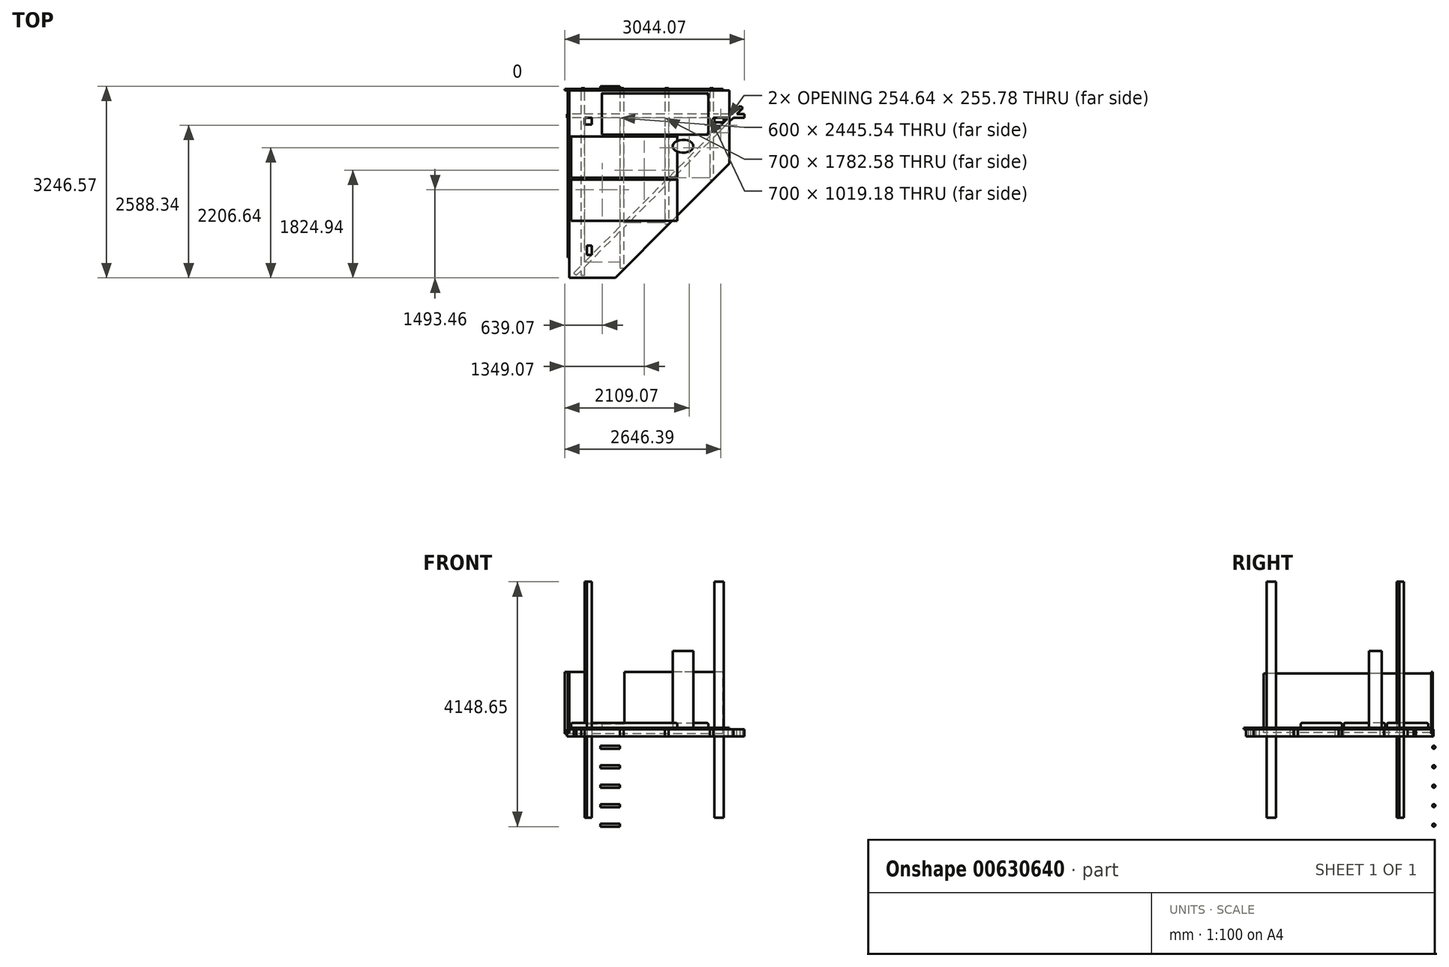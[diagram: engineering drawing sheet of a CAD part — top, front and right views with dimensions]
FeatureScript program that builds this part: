
annotation { "Feature Type Name" : "Feature", "Feature Type Description" : "" }
export const myFeature = defineFeature(function(context is Context, id is Id, definition is map)
    precondition{}
    {
        {
            var Q0;
            Q0=qCreatedBy(makeId("Top.planeOp"),FACE);
            var sketch = newSketch(context, id + "F0", { "sketchPlane" : qUnion([Q0])});
            skLineSegment(sketch, "E0.bottom", {"start": v(0, 0) * mm, "end": v(120, 0) * mm});
            skLineSegment(sketch, "E0.top", {"start": v(0, -120) * mm, "end": v(120, -120) * mm});
            skLineSegment(sketch, "E0.left", {"start": v(0, 0) * mm, "end": v(0, -120) * mm});
            skLineSegment(sketch, "E0.right", {"start": v(120, 0) * mm, "end": v(120, -120) * mm});
            skLineSegment(sketch, "E1.bottom", {"start": v(2200, 0) * mm, "end": v(2355, 0) * mm});
            skLineSegment(sketch, "E1.top", {"start": v(2200, -80) * mm, "end": v(2355, -80) * mm});
            skLineSegment(sketch, "E1.left", {"start": v(2200, 0) * mm, "end": v(2200, -80) * mm});
            skLineSegment(sketch, "E1.right", {"start": v(2355, 0) * mm, "end": v(2355, -80) * mm});
            skLineSegment(sketch, "E2.bottom", {"start": v(40, -2170) * mm, "end": v(120, -2170) * mm});
            skLineSegment(sketch, "E2.top", {"start": v(40, -2325) * mm, "end": v(120, -2325) * mm});
            skLineSegment(sketch, "E2.left", {"start": v(40, -2170) * mm, "end": v(40, -2325) * mm});
            skLineSegment(sketch, "E2.right", {"start": v(120, -2170) * mm, "end": v(120, -2325) * mm});
            skSolve(sketch);
        }
        {
            var Q0;
            Q0=makeQuery(id+"F0.imprint","IMPRINT",FACE,{"disambiguationData":[TD([[makeQuery(id+"F0.imprint","IMPRINT",EDGE,{"derivedFrom":sQuery(id+"F0.wireOp",EDGE,"E2.bottom")}),-1.0]])]});
            var Q1;
            Q1=makeQuery(id+"F0.imprint","IMPRINT",FACE,{"disambiguationData":[TD([[makeQuery(id+"F0.imprint","IMPRINT",EDGE,{"derivedFrom":sQuery(id+"F0.wireOp",EDGE,"E0.bottom")}),-1.0]])]});
            var Q2;
            Q2=makeQuery(id+"F0.imprint","IMPRINT",FACE,{"disambiguationData":[TD([[makeQuery(id+"F0.imprint","IMPRINT",EDGE,{"derivedFrom":sQuery(id+"F0.wireOp",EDGE,"E1.bottom")}),-1.0]])]});
            extrude(context, id + "F1", {"entities" : qUnion([Q0, Q1, Q2]), "depth" : 4000 * mm, "offsetDistance" : 25 * mm});
        }
        {
            var Q0;
            Q0=qCreatedBy(makeId("Top.planeOp"),FACE);
            cPlane(context, id + "F2", {"entities" : qUnion([Q0]), "cplaneType" : CPlaneType.OFFSET, "offset" : 1500 * mm, "width" : 150 * mm, "height" : 150 * mm});
        }
        {
            var Q0;
            Q0=qCreatedBy(id+"F2.planeOp",FACE);
            var sketch = newSketch(context, id + "F3", { "sketchPlane" : qUnion([Q0])});
            skLineSegment(sketch, "E3.bottom", {"start": v(0, -2675) * mm, "end": v(-60, -2675) * mm});
            skLineSegment(sketch, "E3.top", {"start": v(0, 500) * mm, "end": v(-60, 500) * mm});
            skLineSegment(sketch, "E3.left", {"start": v(0, -2675) * mm, "end": v(0, 500) * mm});
            skLineSegment(sketch, "E3.right", {"start": v(-60, -2675) * mm, "end": v(-60, 500) * mm});
            skLineSegment(sketch, "E4.bottom", {"start": v(2705, 0) * mm, "end": v(-300, 0) * mm});
            skLineSegment(sketch, "E4.top", {"start": v(2705, 60) * mm, "end": v(-300, 60) * mm});
            skLineSegment(sketch, "E4.left", {"start": v(2705, 0) * mm, "end": v(2705, 60) * mm});
            skLineSegment(sketch, "E4.right", {"start": v(-300, 0) * mm, "end": v(-300, 60) * mm});
            skLineSegment(sketch, "E5", {"start": v(-182.52, -2628.87) * mm, "end": v(2636.07, 202.33) * mm});
            skLineSegment(sketch, "E6", {"start": v(2636.07, 202.33) * mm, "end": v(2678.6, 160) * mm});
            skLineSegment(sketch, "E7", {"start": v(2678.6, 160) * mm, "end": v(-140, -2671.2) * mm});
            skLineSegment(sketch, "E8", {"start": v(-182.52, -2628.87) * mm, "end": v(-140, -2671.2) * mm});
            skLineSegment(sketch, "E9.bottom", {"start": v(600, 500) * mm, "end": v(660, 500) * mm});
            skLineSegment(sketch, "E9.top", {"start": v(600, -2550) * mm, "end": v(660, -2550) * mm});
            skLineSegment(sketch, "E9.left", {"start": v(600, 500) * mm, "end": v(600, -2550) * mm});
            skLineSegment(sketch, "E9.right", {"start": v(660, 500) * mm, "end": v(660, -2550) * mm});
            skLineSegment(sketch, "E10.bottom", {"start": v(1360, 500) * mm, "end": v(1420, 500) * mm});
            skLineSegment(sketch, "E10.top", {"start": v(1360, -1800) * mm, "end": v(1420, -1800) * mm});
            skLineSegment(sketch, "E10.left", {"start": v(1360, 500) * mm, "end": v(1360, -1800) * mm});
            skLineSegment(sketch, "E10.right", {"start": v(1420, 500) * mm, "end": v(1420, -1800) * mm});
            skLineSegment(sketch, "E11.bottom", {"start": v(2120, 500) * mm, "end": v(2180, 500) * mm});
            skLineSegment(sketch, "E11.top", {"start": v(2120, -1050) * mm, "end": v(2180, -1050) * mm});
            skLineSegment(sketch, "E11.left", {"start": v(2120, 500) * mm, "end": v(2120, -1050) * mm});
            skLineSegment(sketch, "E11.right", {"start": v(2180, 500) * mm, "end": v(2180, -1050) * mm});
            skLineSegment(sketch, "E12", {"start": v(487.83, -2749.25) * mm, "end": v(2859.35, -367.12) * mm, "construction": true});
            skSolve(sketch);
        }
        {
            var Q0;
            {var subQ0=sQuery(id+"F3.wireOp",EDGE,"E7");var subQ1=sQuery(id+"F3.wireOp",EDGE,"E3.left");var subQ2=makeQuery(id+"F3.imprint","INTERSECT",VERTEX,{"derivedFrom":[subQ1,subQ0]});Q0=makeQuery(id+"F3.imprint","IMPRINT",FACE,{"disambiguationData":[TD([[makeQuery(id+"F3.imprint","IMPRINT",EDGE,{"disambiguationData":[TD([[subQ2,-1.0]])],"derivedFrom":subQ1}),1.0]])]});}
            var Q1;
            {var subQ0=sQuery(id+"F3.wireOp",EDGE,"E3.bottom");Q1=makeQuery(id+"F3.imprint","IMPRINT",FACE,{"disambiguationData":[TD([[makeQuery(id+"F3.imprint","IMPRINT",EDGE,{"derivedFrom":subQ0}),-1.0]])]});}
            var Q2;
            {var subQ5=sQuery(id+"F3.wireOp",EDGE,"E8");Q2=makeQuery(id+"F3.imprint","IMPRINT",FACE,{"disambiguationData":[TD([[makeQuery(id+"F3.imprint","IMPRINT",EDGE,{"derivedFrom":subQ5}),1.0]])]});}
            var Q3;
            {var subQ0=sQuery(id+"F3.wireOp",EDGE,"E7");var subQ1=sQuery(id+"F3.wireOp",EDGE,"E3.left");var subQ2=makeQuery(id+"F3.imprint","INTERSECT",VERTEX,{"derivedFrom":[subQ1,subQ0]});Q3=makeQuery(id+"F3.imprint","IMPRINT",FACE,{"disambiguationData":[TD([[makeQuery(id+"F3.imprint","IMPRINT",EDGE,{"disambiguationData":[TD([[subQ2,-1.0]])],"derivedFrom":subQ1}),-1.0]])]});}
            var Q4;
            {var subQ0=sQuery(id+"F3.wireOp",EDGE,"E5");var subQ1=sQuery(id+"F3.wireOp",EDGE,"E3.left");var subQ2=makeQuery(id+"F3.imprint","INTERSECT",VERTEX,{"derivedFrom":[subQ1,subQ0]});Q4=makeQuery(id+"F3.imprint","IMPRINT",FACE,{"disambiguationData":[TD([[makeQuery(id+"F3.imprint","IMPRINT",EDGE,{"disambiguationData":[TD([[subQ2,-1.0]])],"derivedFrom":subQ1}),1.0]])]});}
            var Q5;
            {var subQ0=sQuery(id+"F3.wireOp",EDGE,"E4.top");var subQ1=sQuery(id+"F3.wireOp",EDGE,"E3.left");var subQ2=makeQuery(id+"F3.imprint","INTERSECT",VERTEX,{"derivedFrom":[subQ1,subQ0]});Q5=makeQuery(id+"F3.imprint","IMPRINT",FACE,{"disambiguationData":[TD([[makeQuery(id+"F3.imprint","IMPRINT",EDGE,{"disambiguationData":[TD([[subQ2,1.0]])],"derivedFrom":subQ1}),-1.0]])]});}
            var Q6;
            {var subQ0=sQuery(id+"F3.wireOp",EDGE,"E4.left");Q6=makeQuery(id+"F3.imprint","IMPRINT",FACE,{"disambiguationData":[TD([[makeQuery(id+"F3.imprint","IMPRINT",EDGE,{"derivedFrom":subQ0}),1.0]])]});}
            var Q7;
            {var subQ5=sQuery(id+"F3.wireOp",EDGE,"E6");Q7=makeQuery(id+"F3.imprint","IMPRINT",FACE,{"disambiguationData":[TD([[makeQuery(id+"F3.imprint","IMPRINT",EDGE,{"derivedFrom":subQ5}),-1.0]])]});}
            var Q8;
            {var subQ0=sQuery(id+"F3.wireOp",EDGE,"E7");var subQ1=sQuery(id+"F3.wireOp",EDGE,"E4.bottom");var subQ2=makeQuery(id+"F3.imprint","INTERSECT",VERTEX,{"derivedFrom":[subQ1,subQ0]});Q8=makeQuery(id+"F3.imprint","IMPRINT",FACE,{"disambiguationData":[TD([[makeQuery(id+"F3.imprint","IMPRINT",EDGE,{"disambiguationData":[TD([[subQ2,-1.0]])],"derivedFrom":subQ1}),-1.0]])]});}
            var Q9;
            {var subQ0=sQuery(id+"F3.wireOp",EDGE,"E3.top");Q9=makeQuery(id+"F3.imprint","IMPRINT",FACE,{"disambiguationData":[TD([[makeQuery(id+"F3.imprint","IMPRINT",EDGE,{"derivedFrom":subQ0}),1.0]])]});}
            var Q10;
            {var subQ5=sQuery(id+"F3.wireOp",EDGE,"E4.right");Q10=makeQuery(id+"F3.imprint","IMPRINT",FACE,{"disambiguationData":[TD([[makeQuery(id+"F3.imprint","IMPRINT",EDGE,{"derivedFrom":subQ5}),-1.0]])]});}
            var Q11;
            {var subQ0=sQuery(id+"F3.wireOp",EDGE,"E4.top");var subQ1=sQuery(id+"F3.wireOp",EDGE,"E3.left");var subQ2=makeQuery(id+"F3.imprint","INTERSECT",VERTEX,{"derivedFrom":[subQ1,subQ0]});Q11=makeQuery(id+"F3.imprint","IMPRINT",FACE,{"disambiguationData":[TD([[makeQuery(id+"F3.imprint","IMPRINT",EDGE,{"disambiguationData":[TD([[subQ2,1.0]])],"derivedFrom":subQ1}),1.0]])]});}
            var Q12;
            {var subQ0=sQuery(id+"F3.wireOp",EDGE,"E9.right");var subQ1=sQuery(id+"F3.wireOp",EDGE,"E4.bottom");var subQ2=makeQuery(id+"F3.imprint","INTERSECT",VERTEX,{"derivedFrom":[subQ1,subQ0]});Q12=makeQuery(id+"F3.imprint","IMPRINT",FACE,{"disambiguationData":[TD([[makeQuery(id+"F3.imprint","IMPRINT",EDGE,{"disambiguationData":[TD([[subQ2,-1.0]])],"derivedFrom":subQ1}),1.0]])]});}
            var Q13;
            {var subQ5=sQuery(id+"F3.wireOp",EDGE,"E9.top");Q13=makeQuery(id+"F3.imprint","IMPRINT",FACE,{"disambiguationData":[TD([[makeQuery(id+"F3.imprint","IMPRINT",EDGE,{"derivedFrom":subQ5}),1.0]])]});}
            var Q14;
            {var subQ5=sQuery(id+"F3.wireOp",EDGE,"E10.top");Q14=makeQuery(id+"F3.imprint","IMPRINT",FACE,{"disambiguationData":[TD([[makeQuery(id+"F3.imprint","IMPRINT",EDGE,{"derivedFrom":subQ5}),1.0]])]});}
            var Q15;
            {var subQ0=sQuery(id+"F3.wireOp",EDGE,"E10.right");var subQ1=sQuery(id+"F3.wireOp",EDGE,"E4.bottom");var subQ2=makeQuery(id+"F3.imprint","INTERSECT",VERTEX,{"derivedFrom":[subQ1,subQ0]});Q15=makeQuery(id+"F3.imprint","IMPRINT",FACE,{"disambiguationData":[TD([[makeQuery(id+"F3.imprint","IMPRINT",EDGE,{"disambiguationData":[TD([[subQ2,-1.0]])],"derivedFrom":subQ1}),1.0]])]});}
            var Q16;
            {var subQ0=sQuery(id+"F3.wireOp",EDGE,"E9.right");var subQ1=sQuery(id+"F3.wireOp",EDGE,"E5");var subQ2=makeQuery(id+"F3.imprint","INTERSECT",VERTEX,{"derivedFrom":[subQ1,subQ0]});Q16=makeQuery(id+"F3.imprint","IMPRINT",FACE,{"disambiguationData":[TD([[makeQuery(id+"F3.imprint","IMPRINT",EDGE,{"disambiguationData":[TD([[subQ2,-1.0]])],"derivedFrom":subQ1}),-1.0]])]});}
            var Q17;
            {var subQ0=sQuery(id+"F3.wireOp",EDGE,"E10.right");var subQ1=sQuery(id+"F3.wireOp",EDGE,"E5");var subQ2=makeQuery(id+"F3.imprint","INTERSECT",VERTEX,{"derivedFrom":[subQ1,subQ0]});Q17=makeQuery(id+"F3.imprint","IMPRINT",FACE,{"disambiguationData":[TD([[makeQuery(id+"F3.imprint","IMPRINT",EDGE,{"disambiguationData":[TD([[subQ2,-1.0]])],"derivedFrom":subQ1}),-1.0]])]});}
            var Q18;
            {var subQ5=sQuery(id+"F3.wireOp",EDGE,"E11.top");Q18=makeQuery(id+"F3.imprint","IMPRINT",FACE,{"disambiguationData":[TD([[makeQuery(id+"F3.imprint","IMPRINT",EDGE,{"derivedFrom":subQ5}),1.0]])]});}
            var Q19;
            {var subQ0=sQuery(id+"F3.wireOp",EDGE,"E9.left");var subQ1=sQuery(id+"F3.wireOp",EDGE,"E5");var subQ2=makeQuery(id+"F3.imprint","INTERSECT",VERTEX,{"derivedFrom":[subQ1,subQ0]});Q19=makeQuery(id+"F3.imprint","IMPRINT",FACE,{"disambiguationData":[TD([[makeQuery(id+"F3.imprint","IMPRINT",EDGE,{"disambiguationData":[TD([[subQ2,-1.0]])],"derivedFrom":subQ1}),-1.0]])]});}
            var Q20;
            {var subQ0=sQuery(id+"F3.wireOp",EDGE,"E10.left");var subQ1=sQuery(id+"F3.wireOp",EDGE,"E5");var subQ2=makeQuery(id+"F3.imprint","INTERSECT",VERTEX,{"derivedFrom":[subQ1,subQ0]});Q20=makeQuery(id+"F3.imprint","IMPRINT",FACE,{"disambiguationData":[TD([[makeQuery(id+"F3.imprint","IMPRINT",EDGE,{"disambiguationData":[TD([[subQ2,-1.0]])],"derivedFrom":subQ1}),-1.0]])]});}
            var Q21;
            {var subQ0=sQuery(id+"F3.wireOp",EDGE,"E11.left");var subQ1=sQuery(id+"F3.wireOp",EDGE,"E5");var subQ2=makeQuery(id+"F3.imprint","INTERSECT",VERTEX,{"derivedFrom":[subQ1,subQ0]});Q21=makeQuery(id+"F3.imprint","IMPRINT",FACE,{"disambiguationData":[TD([[makeQuery(id+"F3.imprint","IMPRINT",EDGE,{"disambiguationData":[TD([[subQ2,-1.0]])],"derivedFrom":subQ1}),-1.0]])]});}
            var Q22;
            {var subQ0=sQuery(id+"F3.wireOp",EDGE,"E7");var subQ1=sQuery(id+"F3.wireOp",EDGE,"E4.bottom");var subQ2=makeQuery(id+"F3.imprint","INTERSECT",VERTEX,{"derivedFrom":[subQ1,subQ0]});Q22=makeQuery(id+"F3.imprint","IMPRINT",FACE,{"disambiguationData":[TD([[makeQuery(id+"F3.imprint","IMPRINT",EDGE,{"disambiguationData":[TD([[subQ2,-1.0]])],"derivedFrom":subQ1}),1.0]])]});}
            var Q23;
            {var subQ0=sQuery(id+"F3.wireOp",EDGE,"E5");var subQ1=sQuery(id+"F3.wireOp",EDGE,"E4.bottom");var subQ2=makeQuery(id+"F3.imprint","INTERSECT",VERTEX,{"derivedFrom":[subQ1,subQ0]});Q23=makeQuery(id+"F3.imprint","IMPRINT",FACE,{"disambiguationData":[TD([[makeQuery(id+"F3.imprint","IMPRINT",EDGE,{"disambiguationData":[TD([[subQ2,-1.0]])],"derivedFrom":subQ1}),-1.0]])]});}
            var Q24;
            {var subQ0=sQuery(id+"F3.wireOp",EDGE,"E11.right");var subQ1=sQuery(id+"F3.wireOp",EDGE,"E4.bottom");var subQ2=makeQuery(id+"F3.imprint","INTERSECT",VERTEX,{"derivedFrom":[subQ1,subQ0]});Q24=makeQuery(id+"F3.imprint","IMPRINT",FACE,{"disambiguationData":[TD([[makeQuery(id+"F3.imprint","IMPRINT",EDGE,{"disambiguationData":[TD([[subQ2,-1.0]])],"derivedFrom":subQ1}),-1.0]])]});}
            var Q25;
            {var subQ0=sQuery(id+"F3.wireOp",EDGE,"E11.right");var subQ1=sQuery(id+"F3.wireOp",EDGE,"E4.bottom");var subQ2=makeQuery(id+"F3.imprint","INTERSECT",VERTEX,{"derivedFrom":[subQ1,subQ0]});Q25=makeQuery(id+"F3.imprint","IMPRINT",FACE,{"disambiguationData":[TD([[makeQuery(id+"F3.imprint","IMPRINT",EDGE,{"disambiguationData":[TD([[subQ2,-1.0]])],"derivedFrom":subQ1}),1.0]])]});}
            var Q26;
            {var subQ5=sQuery(id+"F3.wireOp",EDGE,"E11.bottom");Q26=makeQuery(id+"F3.imprint","IMPRINT",FACE,{"disambiguationData":[TD([[makeQuery(id+"F3.imprint","IMPRINT",EDGE,{"derivedFrom":subQ5}),-1.0]])]});}
            var Q27;
            {var subQ5=sQuery(id+"F3.wireOp",EDGE,"E10.bottom");Q27=makeQuery(id+"F3.imprint","IMPRINT",FACE,{"disambiguationData":[TD([[makeQuery(id+"F3.imprint","IMPRINT",EDGE,{"derivedFrom":subQ5}),-1.0]])]});}
            var Q28;
            {var subQ0=sQuery(id+"F3.wireOp",EDGE,"E10.right");var subQ1=sQuery(id+"F3.wireOp",EDGE,"E4.bottom");var subQ2=makeQuery(id+"F3.imprint","INTERSECT",VERTEX,{"derivedFrom":[subQ1,subQ0]});Q28=makeQuery(id+"F3.imprint","IMPRINT",FACE,{"disambiguationData":[TD([[makeQuery(id+"F3.imprint","IMPRINT",EDGE,{"disambiguationData":[TD([[subQ2,-1.0]])],"derivedFrom":subQ1}),-1.0]])]});}
            var Q29;
            {var subQ0=sQuery(id+"F3.wireOp",EDGE,"E10.left");var subQ1=sQuery(id+"F3.wireOp",EDGE,"E4.bottom");var subQ2=makeQuery(id+"F3.imprint","INTERSECT",VERTEX,{"derivedFrom":[subQ1,subQ0]});Q29=makeQuery(id+"F3.imprint","IMPRINT",FACE,{"disambiguationData":[TD([[makeQuery(id+"F3.imprint","IMPRINT",EDGE,{"disambiguationData":[TD([[subQ2,-1.0]])],"derivedFrom":subQ1}),-1.0]])]});}
            var Q30;
            {var subQ0=sQuery(id+"F3.wireOp",EDGE,"E9.right");var subQ1=sQuery(id+"F3.wireOp",EDGE,"E4.bottom");var subQ2=makeQuery(id+"F3.imprint","INTERSECT",VERTEX,{"derivedFrom":[subQ1,subQ0]});Q30=makeQuery(id+"F3.imprint","IMPRINT",FACE,{"disambiguationData":[TD([[makeQuery(id+"F3.imprint","IMPRINT",EDGE,{"disambiguationData":[TD([[subQ2,-1.0]])],"derivedFrom":subQ1}),-1.0]])]});}
            var Q31;
            {var subQ5=sQuery(id+"F3.wireOp",EDGE,"E9.bottom");Q31=makeQuery(id+"F3.imprint","IMPRINT",FACE,{"disambiguationData":[TD([[makeQuery(id+"F3.imprint","IMPRINT",EDGE,{"derivedFrom":subQ5}),-1.0]])]});}
            var Q32;
            {var subQ0=sQuery(id+"F3.wireOp",EDGE,"E11.left");var subQ1=sQuery(id+"F3.wireOp",EDGE,"E4.bottom");var subQ2=makeQuery(id+"F3.imprint","INTERSECT",VERTEX,{"derivedFrom":[subQ1,subQ0]});Q32=makeQuery(id+"F3.imprint","IMPRINT",FACE,{"disambiguationData":[TD([[makeQuery(id+"F3.imprint","IMPRINT",EDGE,{"disambiguationData":[TD([[subQ2,-1.0]])],"derivedFrom":subQ1}),-1.0]])]});}
            extrude(context, id + "F4", {"entities" : qUnion([Q0, Q1, Q2, Q3, Q4, Q5, Q6, Q7, Q8, Q9, Q10, Q11, Q12, Q13, Q14, Q15, Q16, Q17, Q18, Q19, Q20, Q21, Q22, Q23, Q24, Q25, Q26, Q27, Q28, Q29, Q30, Q31, Q32]), "oppositeDirection" : true, "depth" : 120 * mm, "offsetDistance" : 25 * mm});
        }
        {
            var Q0;
            Q0=makeQuery(id+"F4.opExtrude","CAP_FACE",FACE,{"disambiguationData":[OSD([sQuery(id+"F3.wireOp",EDGE,"E3.bottom"),sQuery(id+"F3.wireOp",EDGE,"E3.top"),sQuery(id+"F3.wireOp",EDGE,"E3.left"),sQuery(id+"F3.wireOp",EDGE,"E3.right"),sQuery(id+"F3.wireOp",EDGE,"E4.bottom"),sQuery(id+"F3.wireOp",EDGE,"E4.top"),sQuery(id+"F3.wireOp",EDGE,"E4.left"),sQuery(id+"F3.wireOp",EDGE,"E4.right"),sQuery(id+"F3.wireOp",EDGE,"E5"),sQuery(id+"F3.wireOp",EDGE,"E6"),sQuery(id+"F3.wireOp",EDGE,"E7"),sQuery(id+"F3.wireOp",EDGE,"E8")])],"isStart":true});
            var sketch = newSketch(context, id + "F5", { "sketchPlane" : qUnion([Q0])});
            skLineSegment(sketch, "E13", {"start": v(-260, 460) * mm, "end": v(-260, -2716.23) * mm});
            skLineSegment(sketch, "E14", {"start": v(-260, -2716.23) * mm, "end": v(520.71, -2716.23) * mm});
            skLineSegment(sketch, "E15", {"start": v(520.71, -2716.23) * mm, "end": v(2450.2, -778.11) * mm});
            skLineSegment(sketch, "E16", {"start": v(-260, 460) * mm, "end": v(2450.2, 460) * mm});
            skLineSegment(sketch, "E17", {"start": v(2450.2, 460) * mm, "end": v(2450.2, -778.11) * mm});
            skSolve(sketch);
        }
        {
            var Q0;
            {var subQ0=sQuery(id+"F5.wireOp",EDGE,"E16");var subQ1=sQuery(id+"F5.wireOp",EDGE,"E13");var subQ2=makeQuery(id+"F5.imprint","INTERSECT",VERTEX,{"derivedFrom":[subQ1,subQ0]});Q0=makeQuery(id+"F5.imprint","IMPRINT",FACE,{"disambiguationData":[TD([[makeQuery(id+"F5.imprint","IMPRINT",EDGE,{"disambiguationData":[TD([[subQ2,-1.0]])],"derivedFrom":subQ1}),1.0]])]});}
            var Q1;
            {var subQ0=sQuery(id+"F3.wireOp",EDGE,"E4.right");var subQ8=sQuery(id+"F5.wireOp",EDGE,"E13");var subQ17=sQuery(id+"F3.wireOp",EDGE,"E4.top");var subQ19=makeQuery(id+"F4.opExtrude","CAP_EDGE",EDGE,{"disambiguationData":[OSD([subQ17]),TDD([makeQuery(id+"F3.imprint","IMPRINT",EDGE,{"disambiguationData":[TD([[makeQuery(id+"F3.imprint","INTERSECT",VERTEX,{"derivedFrom":[subQ17,subQ0]}),1.0]])],"derivedFrom":subQ17})])],"isStart":true});var subQ33=makeQuery(id+"F5.imprint","INTERSECT",VERTEX,{"derivedFrom":[subQ19,subQ8]});Q1=makeQuery(id+"F5.imprint","IMPRINT",FACE,{"disambiguationData":[TD([[makeQuery(id+"F5.imprint","IMPRINT",EDGE,{"disambiguationData":[TD([[subQ33,-1.0]])],"derivedFrom":subQ8}),1.0]])]});}
            var Q2;
            {var subQ0=sQuery(id+"F5.wireOp",EDGE,"E17");var subQ1=sQuery(id+"F5.wireOp",EDGE,"E16");var subQ2=makeQuery(id+"F5.imprint","INTERSECT",VERTEX,{"derivedFrom":[subQ1,subQ0]});Q2=makeQuery(id+"F5.imprint","IMPRINT",FACE,{"disambiguationData":[TD([[makeQuery(id+"F5.imprint","IMPRINT",EDGE,{"disambiguationData":[TD([[subQ2,1.0]])],"derivedFrom":subQ1}),-1.0]])]});}
            var Q3;
            {var subQ0=sQuery(id+"F5.wireOp",EDGE,"E14");var subQ1=sQuery(id+"F5.wireOp",EDGE,"E13");var subQ2=makeQuery(id+"F5.imprint","INTERSECT",VERTEX,{"derivedFrom":[subQ1,subQ0]});Q3=makeQuery(id+"F5.imprint","IMPRINT",FACE,{"disambiguationData":[TD([[makeQuery(id+"F5.imprint","IMPRINT",EDGE,{"disambiguationData":[TD([[subQ2,1.0]])],"derivedFrom":subQ1}),1.0]])]});}
            var Q4;
            {var subQ0=sQuery(id+"F5.wireOp",EDGE,"E15");Q4=makeQuery(id+"F5.imprint","IMPRINT",FACE,{"disambiguationData":[TD([[makeQuery(id+"F5.imprint","IMPRINT",EDGE,{"derivedFrom":subQ0}),1.0]])]});}
            var Q5;
            {var subQ1=sQuery(id+"F3.wireOp",EDGE,"E3.left");var subQ3=sQuery(id+"F3.wireOp",EDGE,"E5");var subQ6=makeQuery(id+"F3.imprint","INTERSECT",VERTEX,{"derivedFrom":[subQ1,subQ3]});var subQ7=makeQuery(id+"F4.opExtrude","CAP_EDGE",EDGE,{"disambiguationData":[OSD([subQ1]),TDD([makeQuery(id+"F3.imprint","IMPRINT",EDGE,{"disambiguationData":[TD([[subQ6,-1.0]])],"derivedFrom":subQ1})])],"isStart":true});var subQ9=sQuery(id+"F5.wireOp",EDGE,"E14");var subQ10=makeQuery(id+"F5.imprint","INTERSECT",VERTEX,{"derivedFrom":[subQ7,subQ9]});Q5=makeQuery(id+"F5.imprint","IMPRINT",FACE,{"disambiguationData":[TD([[makeQuery(id+"F5.imprint","IMPRINT",EDGE,{"disambiguationData":[TD([[subQ10,-1.0]])],"derivedFrom":subQ9}),1.0]])]});}
            var Q6;
            {var subQ0=sQuery(id+"F5.wireOp",EDGE,"E14");var subQ1=sQuery(id+"F3.wireOp",EDGE,"E7");var subQ2=sQuery(id+"F3.wireOp",EDGE,"E3.left");var subQ4=makeQuery(id+"F4.opExtrude","CAP_EDGE",EDGE,{"disambiguationData":[OSD([subQ1]),TDD([makeQuery(id+"F3.imprint","IMPRINT",EDGE,{"disambiguationData":[TD([[makeQuery(id+"F3.imprint","INTERSECT",VERTEX,{"derivedFrom":[subQ2,subQ1]}),1.0]])],"derivedFrom":subQ1})])],"isStart":true});var subQ5=makeQuery(id+"F5.imprint","INTERSECT",VERTEX,{"derivedFrom":[subQ4,subQ0]});Q6=makeQuery(id+"F5.imprint","IMPRINT",FACE,{"disambiguationData":[TD([[makeQuery(id+"F5.imprint","IMPRINT",EDGE,{"disambiguationData":[TD([[subQ5,1.0]])],"derivedFrom":subQ0}),1.0]])]});}
            var Q7;
            {var subQ1=sQuery(id+"F3.wireOp",EDGE,"E7");var subQ4=sQuery(id+"F3.wireOp",EDGE,"E10.left");var subQ5=makeQuery(id+"F3.imprint","INTERSECT",VERTEX,{"derivedFrom":[subQ1,subQ4]});var subQ6=makeQuery(id+"F4.opExtrude","CAP_EDGE",EDGE,{"disambiguationData":[OSD([subQ1]),TDD([makeQuery(id+"F3.imprint","IMPRINT",EDGE,{"disambiguationData":[TD([[subQ5,-1.0]])],"derivedFrom":subQ1})])],"isStart":true});Q7=makeQuery(id+"F5.imprint","IMPRINT",FACE,{"disambiguationData":[TD([[makeQuery(id+"F5.imprint","IMPRINT",EDGE,{"derivedFrom":subQ6}),1.0]])]});}
            var Q8;
            {var subQ0=sQuery(id+"F5.wireOp",EDGE,"E14");var subQ1=sQuery(id+"F3.wireOp",EDGE,"E7");var subQ4=makeQuery(id+"F4.opExtrude","CAP_EDGE",EDGE,{"disambiguationData":[OSD([subQ1]),TDD([makeQuery(id+"F3.imprint","IMPRINT",EDGE,{"disambiguationData":[TD([[makeQuery(id+"F3.imprint","INTERSECT",VERTEX,{"derivedFrom":[sQuery(id+"F3.wireOp",EDGE,"E3.left"),subQ1]}),1.0]])],"derivedFrom":subQ1})])],"isStart":true});var subQ5=makeQuery(id+"F5.imprint","INTERSECT",VERTEX,{"derivedFrom":[subQ4,subQ0]});Q8=makeQuery(id+"F5.imprint","IMPRINT",FACE,{"disambiguationData":[TD([[makeQuery(id+"F5.imprint","IMPRINT",EDGE,{"disambiguationData":[TD([[subQ5,-1.0]])],"derivedFrom":subQ0}),1.0]])]});}
            var Q9;
            {var subQ0=sQuery(id+"F3.wireOp",EDGE,"E10.left");var subQ1=sQuery(id+"F3.wireOp",EDGE,"E4.bottom");var subQ2=makeQuery(id+"F3.imprint","INTERSECT",VERTEX,{"derivedFrom":[subQ1,subQ0]});Q9=makeQuery(id+"F5.imprint","IMPRINT",FACE,{"disambiguationData":[TD([[makeQuery(id+"F5.imprint","IMPRINT",EDGE,{"derivedFrom":makeQuery(id+"F4.opExtrude","CAP_EDGE",EDGE,{"disambiguationData":[OSD([subQ1]),TDD([makeQuery(id+"F3.imprint","IMPRINT",EDGE,{"disambiguationData":[TD([[subQ2,-1.0]])],"derivedFrom":subQ1})])],"isStart":true})}),1.0]])]});}
            var Q10;
            {var subQ0=sQuery(id+"F3.wireOp",EDGE,"E11.left");var subQ1=sQuery(id+"F3.wireOp",EDGE,"E4.bottom");var subQ2=makeQuery(id+"F3.imprint","INTERSECT",VERTEX,{"derivedFrom":[subQ1,subQ0]});Q10=makeQuery(id+"F5.imprint","IMPRINT",FACE,{"disambiguationData":[TD([[makeQuery(id+"F5.imprint","IMPRINT",EDGE,{"derivedFrom":makeQuery(id+"F4.opExtrude","CAP_EDGE",EDGE,{"disambiguationData":[OSD([subQ1]),TDD([makeQuery(id+"F3.imprint","IMPRINT",EDGE,{"disambiguationData":[TD([[subQ2,-1.0]])],"derivedFrom":subQ1})])],"isStart":true})}),1.0]])]});}
            var Q11;
            {var subQ2=sQuery(id+"F3.wireOp",EDGE,"E4.top");var subQ6=sQuery(id+"F3.wireOp",EDGE,"E11.left");var subQ7=makeQuery(id+"F3.imprint","INTERSECT",VERTEX,{"derivedFrom":[subQ2,subQ6]});var subQ10=makeQuery(id+"F4.opExtrude","CAP_EDGE",EDGE,{"disambiguationData":[OSD([subQ2]),TDD([makeQuery(id+"F3.imprint","IMPRINT",EDGE,{"disambiguationData":[TD([[subQ7,-1.0]])],"derivedFrom":subQ2})])],"isStart":true});Q11=makeQuery(id+"F5.imprint","IMPRINT",FACE,{"disambiguationData":[TD([[makeQuery(id+"F5.imprint","IMPRINT",EDGE,{"derivedFrom":subQ10}),-1.0]])]});}
            var Q12;
            {var subQ2=sQuery(id+"F3.wireOp",EDGE,"E4.top");var subQ6=sQuery(id+"F3.wireOp",EDGE,"E10.left");var subQ7=makeQuery(id+"F3.imprint","INTERSECT",VERTEX,{"derivedFrom":[subQ2,subQ6]});var subQ10=makeQuery(id+"F4.opExtrude","CAP_EDGE",EDGE,{"disambiguationData":[OSD([subQ2]),TDD([makeQuery(id+"F3.imprint","IMPRINT",EDGE,{"disambiguationData":[TD([[subQ7,-1.0]])],"derivedFrom":subQ2})])],"isStart":true});Q12=makeQuery(id+"F5.imprint","IMPRINT",FACE,{"disambiguationData":[TD([[makeQuery(id+"F5.imprint","IMPRINT",EDGE,{"derivedFrom":subQ10}),-1.0]])]});}
            var Q13;
            {var subQ1=sQuery(id+"F3.wireOp",EDGE,"E3.left");var subQ2=sQuery(id+"F3.wireOp",EDGE,"E4.top");var subQ3=makeQuery(id+"F3.imprint","INTERSECT",VERTEX,{"derivedFrom":[subQ1,subQ2]});var subQ10=makeQuery(id+"F4.opExtrude","CAP_EDGE",EDGE,{"disambiguationData":[OSD([subQ2]),TDD([makeQuery(id+"F3.imprint","IMPRINT",EDGE,{"disambiguationData":[TD([[subQ3,1.0]])],"derivedFrom":subQ2})])],"isStart":true});Q13=makeQuery(id+"F5.imprint","IMPRINT",FACE,{"disambiguationData":[TD([[makeQuery(id+"F5.imprint","IMPRINT",EDGE,{"derivedFrom":subQ10}),-1.0]])]});}
            var Q14;
            {var subQ0=sQuery(id+"F3.wireOp",EDGE,"E5");var subQ1=sQuery(id+"F3.wireOp",EDGE,"E3.left");var subQ2=makeQuery(id+"F3.imprint","INTERSECT",VERTEX,{"derivedFrom":[subQ1,subQ0]});Q14=makeQuery(id+"F5.imprint","IMPRINT",FACE,{"disambiguationData":[TD([[makeQuery(id+"F5.imprint","IMPRINT",EDGE,{"derivedFrom":makeQuery(id+"F4.opExtrude","CAP_EDGE",EDGE,{"disambiguationData":[OSD([subQ1]),TDD([makeQuery(id+"F3.imprint","IMPRINT",EDGE,{"disambiguationData":[TD([[subQ2,-1.0]])],"derivedFrom":subQ1})])],"isStart":true})}),-1.0]])]});}
            extrude(context, id + "F6", {"entities" : qUnion([Q0, Q1, Q2, Q3, Q4, Q5, Q6, Q7, Q8, Q9, Q10, Q11, Q12, Q13, Q14]), "depth" : 25 * mm, "offsetDistance" : 25 * mm});
        }
        {
            var Q0;
            Q0=makeQuery(id+"F6.opExtrude","CAP_FACE",FACE,{"disambiguationData":[OSD([sQuery(id+"F5.wireOp",EDGE,"E13"),sQuery(id+"F5.wireOp",EDGE,"E14"),sQuery(id+"F5.wireOp",EDGE,"E15"),sQuery(id+"F5.wireOp",EDGE,"E16"),sQuery(id+"F5.wireOp",EDGE,"E17")])],"isStart":false});
            var sketch = newSketch(context, id + "F7", { "sketchPlane" : qUnion([Q0])});
            skLineSegment(sketch, "E18.bottom", {"start": v(292.62, 410) * mm, "end": v(2092.62, 410) * mm});
            skLineSegment(sketch, "E18.top", {"start": v(292.62, -290) * mm, "end": v(2092.62, -290) * mm});
            skLineSegment(sketch, "E18.left", {"start": v(292.62, 410) * mm, "end": v(292.62, -290) * mm});
            skLineSegment(sketch, "E18.right", {"start": v(2092.62, 410) * mm, "end": v(2092.62, -290) * mm});
            skLineSegment(sketch, "E19.bottom", {"start": v(-230, -320) * mm, "end": v(1570, -320) * mm});
            skLineSegment(sketch, "E19.top", {"start": v(-230, -1020) * mm, "end": v(1570, -1020) * mm});
            skLineSegment(sketch, "E19.left", {"start": v(-230, -320) * mm, "end": v(-230, -1020) * mm});
            skLineSegment(sketch, "E19.right", {"start": v(1570, -320) * mm, "end": v(1570, -1020) * mm});
            skLineSegment(sketch, "E20.bottom", {"start": v(-230, -1050) * mm, "end": v(1570, -1050) * mm});
            skLineSegment(sketch, "E20.top", {"start": v(-230, -1750) * mm, "end": v(1570, -1750) * mm});
            skLineSegment(sketch, "E20.left", {"start": v(-230, -1050) * mm, "end": v(-230, -1750) * mm});
            skLineSegment(sketch, "E20.right", {"start": v(1570, -1050) * mm, "end": v(1570, -1750) * mm});
            skSolve(sketch);
        }
        {
            var Q0;
            Q0=makeQuery(id+"F7.imprint","IMPRINT",FACE,{"disambiguationData":[TD([[makeQuery(id+"F7.imprint","IMPRINT",EDGE,{"derivedFrom":sQuery(id+"F7.wireOp",EDGE,"E18.bottom")}),-1.0]])]});
            var Q1;
            Q1=makeQuery(id+"F7.imprint","IMPRINT",FACE,{"disambiguationData":[TD([[makeQuery(id+"F7.imprint","IMPRINT",EDGE,{"derivedFrom":sQuery(id+"F7.wireOp",EDGE,"E19.bottom")}),-1.0]])]});
            var Q2;
            {var subQ1=sQuery(id+"F7.wireOp",EDGE,"E20.bottom");Q2=makeQuery(id+"F7.imprint","IMPRINT",FACE,{"disambiguationData":[TD([[makeQuery(id+"F7.imprint","IMPRINT",EDGE,{"derivedFrom":subQ1}),-1.0]])]});}
            var Q3;
            {var subQ0=sQuery(id+"F7.wireOp",EDGE,"E20.right");var subQ1=sQuery(id+"F7.wireOp",EDGE,"E20.top");var subQ2=makeQuery(id+"F7.imprint","INTERSECT",VERTEX,{"derivedFrom":[subQ1,subQ0]});Q3=makeQuery(id+"F7.imprint","IMPRINT",FACE,{"disambiguationData":[TD([[makeQuery(id+"F7.imprint","IMPRINT",EDGE,{"disambiguationData":[TD([[subQ2,1.0]])],"derivedFrom":subQ1}),1.0]])]});}
            extrude(context, id + "F8", {"entities" : qUnion([Q0, Q1, Q2, Q3]), "depth" : 80 * mm, "offsetDistance" : 25 * mm});
        }
        {
            var Q0;
            Q0=makeQuery(id+"F8.opExtrude","CAP_EDGE",EDGE,{"disambiguationData":[OSD([sQuery(id+"F7.wireOp",EDGE,"E20.top")])],"isStart":false});
            var Q1;
            Q1=makeQuery(id+"F8.opExtrude","CAP_EDGE",EDGE,{"disambiguationData":[OSD([sQuery(id+"F7.wireOp",EDGE,"E20.left")])],"isStart":false});
            var Q2;
            Q2=makeQuery(id+"F8.opExtrude","CAP_EDGE",EDGE,{"disambiguationData":[OSD([sQuery(id+"F7.wireOp",EDGE,"E20.bottom")])],"isStart":false});
            var Q3;
            Q3=makeQuery(id+"F8.opExtrude","CAP_EDGE",EDGE,{"disambiguationData":[OSD([sQuery(id+"F7.wireOp",EDGE,"E20.right")])],"isStart":false});
            var Q4;
            Q4=makeQuery(id+"F8.opExtrude","CAP_EDGE",EDGE,{"disambiguationData":[OSD([sQuery(id+"F7.wireOp",EDGE,"E19.top")])],"isStart":false});
            var Q5;
            Q5=makeQuery(id+"F8.opExtrude","CAP_EDGE",EDGE,{"disambiguationData":[OSD([sQuery(id+"F7.wireOp",EDGE,"E19.right")])],"isStart":false});
            var Q6;
            Q6=makeQuery(id+"F8.opExtrude","CAP_EDGE",EDGE,{"disambiguationData":[OSD([sQuery(id+"F7.wireOp",EDGE,"E19.bottom")])],"isStart":false});
            var Q7;
            Q7=makeQuery(id+"F8.opExtrude","CAP_EDGE",EDGE,{"disambiguationData":[OSD([sQuery(id+"F7.wireOp",EDGE,"E19.left")])],"isStart":false});
            var Q8;
            Q8=makeQuery(id+"F8.opExtrude","CAP_EDGE",EDGE,{"disambiguationData":[OSD([sQuery(id+"F7.wireOp",EDGE,"E18.top")])],"isStart":false});
            var Q9;
            Q9=makeQuery(id+"F8.opExtrude","CAP_EDGE",EDGE,{"disambiguationData":[OSD([sQuery(id+"F7.wireOp",EDGE,"E18.left")])],"isStart":false});
            var Q10;
            Q10=makeQuery(id+"F8.opExtrude","CAP_EDGE",EDGE,{"disambiguationData":[OSD([sQuery(id+"F7.wireOp",EDGE,"E18.bottom")])],"isStart":false});
            var Q11;
            Q11=makeQuery(id+"F8.opExtrude","CAP_EDGE",EDGE,{"disambiguationData":[OSD([sQuery(id+"F7.wireOp",EDGE,"E18.right")])],"isStart":false});
            fillet(context, id + "F9", {"entities" : qUnion([Q0, Q1, Q2, Q3, Q4, Q5, Q6, Q7, Q8, Q9, Q10, Q11]), "radius" : 20 * mm, "tangentPropagation" : true, "allowEdgeOverflow" : false});
        }
        {
            var Q0;
            Q0=makeQuery(id+"F6.opExtrude","CAP_FACE",FACE,{"disambiguationData":[OSD([sQuery(id+"F5.wireOp",EDGE,"E13"),sQuery(id+"F5.wireOp",EDGE,"E14"),sQuery(id+"F5.wireOp",EDGE,"E15"),sQuery(id+"F5.wireOp",EDGE,"E16"),sQuery(id+"F5.wireOp",EDGE,"E17")])],"isStart":false});
            cPlane(context, id + "F10", {"entities" : qUnion([Q0]), "cplaneType" : CPlaneType.OFFSET, "offset" : 1000 * mm, "width" : 150 * mm, "height" : 150 * mm});
        }
        {
            var Q0;
            Q0=qCreatedBy(id+"F10.planeOp",FACE);
            var sketch = newSketch(context, id + "F11", { "sketchPlane" : qUnion([Q0])});
            skLineSegment(sketch, "E21.bottom", {"start": v(0, 200) * mm, "end": v(-60, 200) * mm});
            skLineSegment(sketch, "E21.top", {"start": v(0, -2525) * mm, "end": v(-60, -2525) * mm});
            skLineSegment(sketch, "E21.left", {"start": v(0, 200) * mm, "end": v(0, -2525) * mm});
            skLineSegment(sketch, "E21.right", {"start": v(-60, 200) * mm, "end": v(-60, -2525) * mm});
            skSolve(sketch);
        }
        {
            var Q0;
            Q0=makeQuery(id+"F6.opExtrude","CAP_FACE",FACE,{"disambiguationData":[OSD([sQuery(id+"F5.wireOp",EDGE,"E13"),sQuery(id+"F5.wireOp",EDGE,"E14"),sQuery(id+"F5.wireOp",EDGE,"E15"),sQuery(id+"F5.wireOp",EDGE,"E16"),sQuery(id+"F5.wireOp",EDGE,"E17")])],"isStart":false});
            var sketch = newSketch(context, id + "F12", { "sketchPlane" : qUnion([Q0])});
            skEllipse(sketch, "E22", {"center": v(1667.97, -484.93) * mm, "majorRadius": 175 * mm, "minorRadius": 110 * mm, "majorAxis": v(1, 0)});
            skSolve(sketch);
        }
        {
            var Q0;
            Q0=makeQuery(id+"F12.imprint","IMPRINT",FACE,{"disambiguationData":[TD([[makeQuery(id+"F12.imprint","IMPRINT",EDGE,{"derivedFrom":sQuery(id+"F12.wireOp",EDGE,"E22")}),1.0]])]});
            extrude(context, id + "F13", {"entities" : qUnion([Q0]), "depth" : 1300 * mm, "offsetDistance" : 25 * mm});
        }
        {
            var Q0;
            Q0=makeQuery(id+"F6.opExtrude","SWEPT_FACE",FACE,{"disambiguationData":[OSD([sQuery(id+"F5.wireOp",EDGE,"E16")])]});
            var sketch = newSketch(context, id + "F14", { "sketchPlane" : qUnion([Q0])});
            skLineSegment(sketch, "E23.bottom", {"start": v(-2341.2, 1426.19) * mm, "end": v(339.07, 1426.19) * mm});
            skLineSegment(sketch, "E23.top", {"start": v(-2341.2, 2473.16) * mm, "end": v(339.07, 2473.16) * mm});
            skLineSegment(sketch, "E23.left", {"start": v(-2341.2, 1426.19) * mm, "end": v(-2341.2, 2473.16) * mm});
            skLineSegment(sketch, "E23.right", {"start": v(339.07, 1426.19) * mm, "end": v(339.07, 2473.16) * mm});
            skSolve(sketch);
        }
        {
            var Q0;
            Q0=makeQuery(id+"F14.imprint","IMPRINT",FACE,{"disambiguationData":[TD([[makeQuery(id+"F14.imprint","IMPRINT",EDGE,{"derivedFrom":sQuery(id+"F14.wireOp",EDGE,"E23.bottom")}),1.0]])]});
            extrude(context, id + "F15", {"entities" : qUnion([Q0]), "depth" : 25 * mm, "offsetDistance" : 25 * mm});
        }
        {
            var Q0;
            Q0=makeQuery(id+"F6.opExtrude","SWEPT_FACE",FACE,{"disambiguationData":[OSD([sQuery(id+"F5.wireOp",EDGE,"E13")])]});
            var sketch = newSketch(context, id + "F16", { "sketchPlane" : qUnion([Q0])});
            skLineSegment(sketch, "E24.bottom", {"start": v(-460.23, 1443.42) * mm, "end": v(2374.6, 1443.42) * mm});
            skLineSegment(sketch, "E24.top", {"start": v(-460.23, 2447.85) * mm, "end": v(2374.6, 2447.85) * mm});
            skLineSegment(sketch, "E24.left", {"start": v(-460.23, 1443.42) * mm, "end": v(-460.23, 2447.85) * mm});
            skLineSegment(sketch, "E24.right", {"start": v(2374.6, 1443.42) * mm, "end": v(2374.6, 2447.85) * mm});
            skSolve(sketch);
        }
        {
            var Q0;
            Q0=makeQuery(id+"F16.imprint","IMPRINT",FACE,{"disambiguationData":[TD([[makeQuery(id+"F16.imprint","IMPRINT",EDGE,{"derivedFrom":sQuery(id+"F16.wireOp",EDGE,"E24.bottom")}),1.0]])]});
            extrude(context, id + "F17", {"entities" : qUnion([Q0]), "depth" : 25 * mm, "offsetDistance" : 25 * mm});
        }
        {
            var Q0;
            Q0=makeQuery(id+"F6.opExtrude","SWEPT_FACE",FACE,{"disambiguationData":[OSD([sQuery(id+"F5.wireOp",EDGE,"E15")])]});
            var sketch = newSketch(context, id + "F18", { "sketchPlane" : qUnion([Q0])});
            skLineSegment(sketch, "E25.bottom", {"start": v(-1428.21, 1536.93) * mm, "end": v(1570, 1536.93) * mm});
            skLineSegment(sketch, "E25.top", {"start": v(-1428.21, 2600.55) * mm, "end": v(1570, 2600.55) * mm});
            skLineSegment(sketch, "E25.left", {"start": v(-1428.21, 1536.93) * mm, "end": v(-1428.21, 2600.55) * mm});
            skLineSegment(sketch, "E25.right", {"start": v(1570, 1536.93) * mm, "end": v(1570, 2600.55) * mm});
            skSolve(sketch);
        }
        {
            var Q0;
            Q0=makeQuery(id+"F1.opExtrude","CAP_FACE",FACE,{"disambiguationData":[OSD([sQuery(id+"F0.wireOp",EDGE,"E2.bottom"),sQuery(id+"F0.wireOp",EDGE,"E2.top"),sQuery(id+"F0.wireOp",EDGE,"E2.left"),sQuery(id+"F0.wireOp",EDGE,"E2.right")])],"isStart":false});
            var sketch = newSketch(context, id + "F19", { "sketchPlane" : qUnion([Q0])});
            skLineSegment(sketch, "E26", {"start": v(-401.05, -2498.73) * mm, "end": v(-583.17, 556.79) * mm});
            skLineSegment(sketch, "E27", {"start": v(-583.17, 556.79) * mm, "end": v(2634.23, 556.79) * mm});
            skLineSegment(sketch, "E28", {"start": v(2634.23, 556.79) * mm, "end": v(2452.11, -1056.97) * mm});
            skLineSegment(sketch, "E29", {"start": v(2452.11, -1056.97) * mm, "end": v(959.77, -2635.32) * mm});
            skLineSegment(sketch, "E30", {"start": v(959.77, -2635.32) * mm, "end": v(-401.05, -2498.73) * mm});
            skSolve(sketch);
        }
        {
            var Q0;
            Q0=makeQuery(id+"F8.opExtrude","CAP_FACE",FACE,{"disambiguationData":[OSD([sQuery(id+"F7.wireOp",EDGE,"E19.bottom"),sQuery(id+"F7.wireOp",EDGE,"E19.top"),sQuery(id+"F7.wireOp",EDGE,"E19.left"),sQuery(id+"F7.wireOp",EDGE,"E19.right")])],"isStart":false});
            var sketch = newSketch(context, id + "F20", { "sketchPlane" : qUnion([Q0])});
            skEllipse(sketch, "E31", {"center": v(685.84, -526.18) * mm, "majorRadius": 275 * mm, "minorRadius": 125 * mm, "majorAxis": v(0.93, -0.38)});
            skSolve(sketch);
        }
        {
            var Q0;
            Q0=makeQuery(id+"F15.opExtrude","CAP_FACE",FACE,{"disambiguationData":[OSD([sQuery(id+"F5.wireOp",EDGE,"E13"),sQuery(id+"F5.wireOp",EDGE,"E16"),sQuery(id+"F14.wireOp",EDGE,"E23.bottom"),sQuery(id+"F14.wireOp",EDGE,"E23.top"),sQuery(id+"F14.wireOp",EDGE,"E23.left"),sQuery(id+"F14.wireOp",EDGE,"E23.right")])],"isStart":false});
            var sketch = newSketch(context, id + "F21", { "sketchPlane" : qUnion([Q0])});
            skLineSegment(sketch, "E32.bottom", {"start": v(-673.28, 2611.78) * mm, "end": v(0, 2611.78) * mm});
            skLineSegment(sketch, "E32.top", {"start": v(-673.28, 1585.92) * mm, "end": v(0, 1585.92) * mm});
            skLineSegment(sketch, "E32.left", {"start": v(-673.28, 2611.78) * mm, "end": v(-673.28, 1585.92) * mm});
            skLineSegment(sketch, "E32.right", {"start": v(0, 2611.78) * mm, "end": v(0, 1585.92) * mm});
            skSolve(sketch);
        }
        {
            var Q0;
            {var subQ0=sQuery(id+"F21.wireOp",EDGE,"E32.top");Q0=makeQuery(id+"F21.imprint","IMPRINT",FACE,{"disambiguationData":[TD([[makeQuery(id+"F21.imprint","IMPRINT",EDGE,{"derivedFrom":subQ0}),1.0]])]});}
            extrude(context, id + "F22", {"entities" : qUnion([Q0]), "operationType" : NewBodyOperationType.REMOVE, "oppositeDirection" : true, "depth" : 25 * mm, "offsetDistance" : 25 * mm});
        }
        {
            var Q0;
            {var subQ0=sQuery(id+"F3.wireOp",EDGE,"E9.left");Q0=makeQuery(id+"F4.opExtrude","SWEPT_FACE",FACE,{"disambiguationData":[OSD([subQ0]),TDD([makeQuery(id+"F3.imprint","IMPRINT",EDGE,{"disambiguationData":[TD([[makeQuery(id+"F3.imprint","INTERSECT",VERTEX,{"derivedFrom":[sQuery(id+"F3.wireOp",EDGE,"E9.bottom"),subQ0]}),-1.0]])],"derivedFrom":subQ0})])]});}
            var sketch = newSketch(context, id + "F23", { "sketchPlane" : qUnion([Q0])});
            skCircle(sketch, "E33", {"center": v(-505.34, 1196.35) * mm, "radius": 25 * mm});
            skCircle(sketch, "E34.0.1.0", {"center": v(-505.34, 866.35) * mm, "radius": 25 * mm});
            skCircle(sketch, "E34.0.2.0", {"center": v(-505.34, 536.35) * mm, "radius": 25 * mm});
            skCircle(sketch, "E34.0.3.0", {"center": v(-505.34, 206.35) * mm, "radius": 25 * mm});
            skCircle(sketch, "E34.0.4.0", {"center": v(-505.34, -123.65) * mm, "radius": 25 * mm});
            skLineSegment(sketch, "E34.direction1", {"start": v(-505.34, 1196.35) * mm, "end": v(-422.34, 1196.35) * mm, "construction": true});
            skLineSegment(sketch, "E34.direction2", {"start": v(-505.34, 1196.35) * mm, "end": v(-505.34, 866.35) * mm, "construction": true});
            skSolve(sketch);
        }
        {
            var Q0;
            Q0=makeQuery(id+"F23.imprint","IMPRINT",FACE,{"disambiguationData":[TD([[makeQuery(id+"F23.imprint","IMPRINT",EDGE,{"derivedFrom":sQuery(id+"F23.wireOp",EDGE,"E33")}),1.0]])]});
            var Q1;
            Q1=makeQuery(id+"F23.imprint","IMPRINT",FACE,{"disambiguationData":[TD([[makeQuery(id+"F23.imprint","IMPRINT",EDGE,{"derivedFrom":sQuery(id+"F23.wireOp",EDGE,"E34.0.1.0")}),1.0]])]});
            var Q2;
            Q2=makeQuery(id+"F23.imprint","IMPRINT",FACE,{"disambiguationData":[TD([[makeQuery(id+"F23.imprint","IMPRINT",EDGE,{"derivedFrom":sQuery(id+"F23.wireOp",EDGE,"E34.0.2.0")}),1.0]])]});
            var Q3;
            Q3=makeQuery(id+"F23.imprint","IMPRINT",FACE,{"disambiguationData":[TD([[makeQuery(id+"F23.imprint","IMPRINT",EDGE,{"derivedFrom":sQuery(id+"F23.wireOp",EDGE,"E34.0.3.0")}),1.0]])]});
            var Q4;
            Q4=makeQuery(id+"F23.imprint","IMPRINT",FACE,{"disambiguationData":[TD([[makeQuery(id+"F23.imprint","IMPRINT",EDGE,{"derivedFrom":sQuery(id+"F23.wireOp",EDGE,"E34.0.4.0")}),1.0]])]});
            extrude(context, id + "F24", {"entities" : qUnion([Q0, Q1, Q2, Q3, Q4]), "depth" : 330 * mm, "offsetDistance" : 25 * mm});
        }
    });
